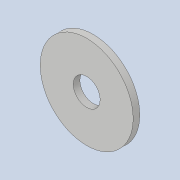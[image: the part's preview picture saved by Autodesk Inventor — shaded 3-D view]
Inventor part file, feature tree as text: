
AUTODESK INVENTOR PART (.ipt)
format: ipt  version: 2020.4 (Build 244396000, 396)  size: 95,744 bytes
history: native  units: mm
features: extrude x1, sketch x1
ambient origin geometry x8: Origin, YZ Plane, XZ Plane, XY Plane, X Axis, Y Axis, Z Axis, Center Point
bodies: Solid1 (feature_tree)
feature tree (2):
  extrude  "Extrusion1"  Depth=1.0mm
  sketch  "Sketch1"  dims[d0=14.0mm d1=4.05mm d2=1.0mm d3=0.0mm]
